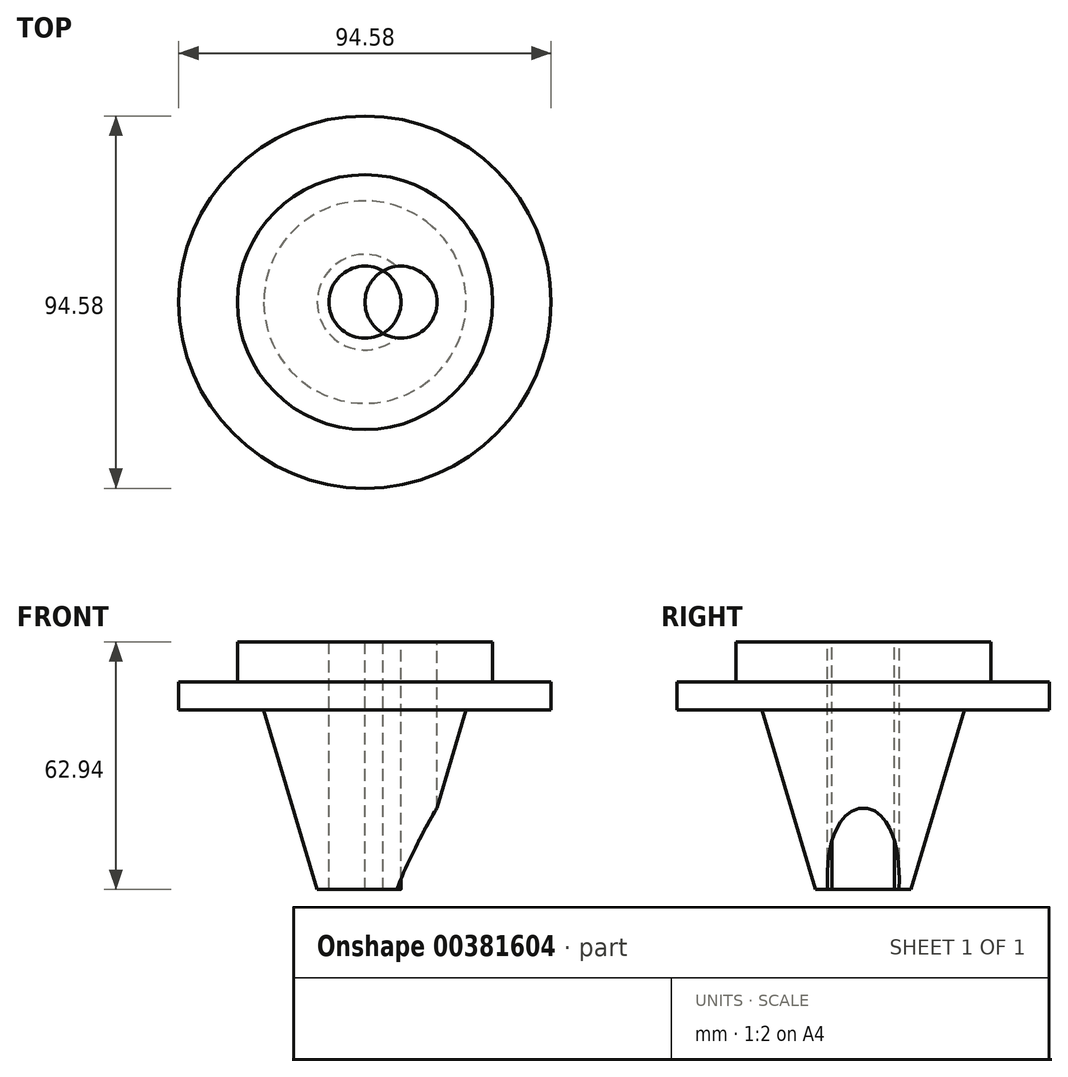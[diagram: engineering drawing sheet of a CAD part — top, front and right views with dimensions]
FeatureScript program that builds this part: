
annotation { "Feature Type Name" : "Feature", "Feature Type Description" : "" }
export const myFeature = defineFeature(function(context is Context, id is Id, definition is map)
    precondition{}
    {
        {
            var Q0;
            Q0=qCreatedBy(makeId("Front.planeOp"),FACE);
            var sketch = newSketch(context, id + "F0", { "sketchPlane" : qUnion([Q0])});
            skLineSegment(sketch, "E0", {"start": v(0, 0) * mm, "end": v(0, 62.94) * mm});
            skLineSegment(sketch, "E1", {"start": v(0, 62.94) * mm, "end": v(32.38, 62.94) * mm});
            skLineSegment(sketch, "E2", {"start": v(32.38, 62.94) * mm, "end": v(32.38, 52.76) * mm});
            skLineSegment(sketch, "E3", {"start": v(32.38, 52.76) * mm, "end": v(47.29, 52.76) * mm});
            skLineSegment(sketch, "E4", {"start": v(47.29, 52.76) * mm, "end": v(47.29, 45.65) * mm});
            skLineSegment(sketch, "E5", {"start": v(47.29, 45.65) * mm, "end": v(25.72, 45.65) * mm});
            skLineSegment(sketch, "E6", {"start": v(25.72, 45.65) * mm, "end": v(12.14, 0) * mm});
            skLineSegment(sketch, "E7", {"start": v(12.14, 0) * mm, "end": v(0, 0) * mm});
            skSolve(sketch);
        }
        {
            var Q0;
            Q0 = qSketchRegion(id + "F0", true);
            var Q1;
            Q1=sQuery(id+"F0.wireOp",EDGE,"E0");
            revolve(context, id + "F1", {"entities" : qUnion([Q0]), "axis" : qUnion([Q1]), "revolveType" : RevolveType.FULL});
        }
        {
            var Q0;
            Q0=makeQuery(id+"F1.opRevolve","SWEPT_FACE",FACE,{"disambiguationData":[OSD([sQuery(id+"F0.wireOp",EDGE,"E1")])]});
            var sketch = newSketch(context, id + "F2", { "sketchPlane" : qUnion([Q0])});
            skCircle(sketch, "E8", {"center": v(0, 0) * mm, "radius": 9.15 * mm});
            skCircle(sketch, "E9", {"center": v(9.15, 0) * mm, "radius": 9.15 * mm});
            skSolve(sketch);
        }
        {
            var Q0;
            {var subQ0=sQuery(id+"F2.wireOp",EDGE,"E9");var subQ1=sQuery(id+"F2.wireOp",EDGE,"E8");var subQ2=makeQuery(id+"F2.imprint","INTERSECT",VERTEX,{"disambiguationData":[OD(0.0)],"derivedFrom":[subQ1,subQ0]});Q0=makeQuery(id+"F2.imprint","IMPRINT",FACE,{"disambiguationData":[TD([[makeQuery(id+"F2.imprint","IMPRINT",EDGE,{"disambiguationData":[TD([[subQ2,1.0]])],"derivedFrom":subQ1}),1.0]])]});}
            var Q1;
            {var subQ0=sQuery(id+"F2.wireOp",EDGE,"E9");var subQ1=sQuery(id+"F2.wireOp",EDGE,"E8");var subQ2=makeQuery(id+"F2.imprint","INTERSECT",VERTEX,{"disambiguationData":[OD(0.0)],"derivedFrom":[subQ1,subQ0]});Q1=makeQuery(id+"F2.imprint","IMPRINT",FACE,{"disambiguationData":[TD([[makeQuery(id+"F2.imprint","IMPRINT",EDGE,{"disambiguationData":[TD([[subQ2,-1.0]])],"derivedFrom":subQ1}),-1.0]])]});}
            extrude(context, id + "F3", {"entities" : qUnion([Q0, Q1]), "operationType" : NewBodyOperationType.REMOVE, "oppositeDirection" : true, "depth" : 127 * mm});
        }
    });
